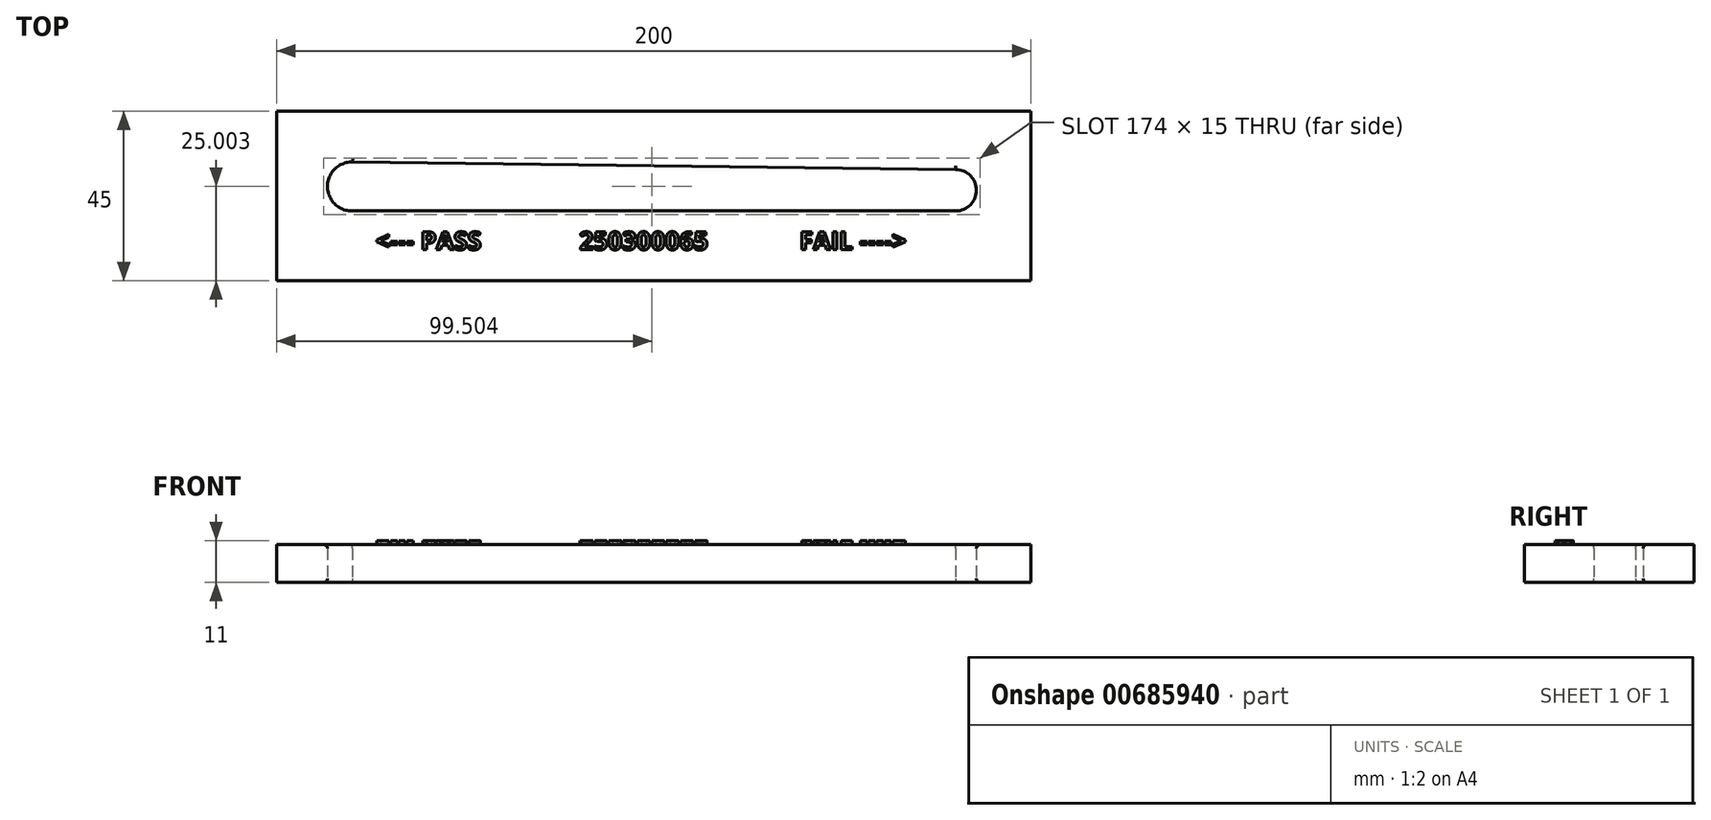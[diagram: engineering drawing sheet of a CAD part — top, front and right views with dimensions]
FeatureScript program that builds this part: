
annotation { "Feature Type Name" : "Feature", "Feature Type Description" : "" }
export const myFeature = defineFeature(function(context is Context, id is Id, definition is map)
    precondition{}
    {
        {
            var Q0;
            Q0=qCreatedBy(makeId("Top.planeOp"),FACE);
            var sketch = newSketch(context, id + "F0", { "sketchPlane" : qUnion([Q0])});
            skLineSegment(sketch, "E0", {"start": v(-35.7, 23.28) * mm, "end": v(124.3, 21.28) * mm});
            skLineSegment(sketch, "E1", {"start": v(-35.7, 10.28) * mm, "end": v(124.3, 10.28) * mm});
            skArc(sketch, "E2", {"start": v(-35.54, 23.28) * mm, "mid": v(-42.2, 16.87) * mm, "end": v(-35.7, 10.28) * mm});
            skArc(sketch, "E3", {"start": v(124.3, 10.28) * mm, "mid": v(129.8, 15.78) * mm, "end": v(124.3, 21.28) * mm});
            skLineSegment(sketch, "E4.bottom", {"start": v(-55.7, 36.78) * mm, "end": v(144.3, 36.78) * mm});
            skLineSegment(sketch, "E4.top", {"start": v(-55.7, -8.22) * mm, "end": v(144.3, -8.22) * mm});
            skLineSegment(sketch, "E4.left", {"start": v(-55.7, 36.78) * mm, "end": v(-55.7, -8.22) * mm});
            skLineSegment(sketch, "E4.right", {"start": v(144.3, 36.78) * mm, "end": v(144.3, -8.22) * mm});
            skSolve(sketch);
        }
        {
            var Q0;
            Q0 = qSketchRegion(id + "F0", true);
            extrude(context, id + "F1", {"entities" : qUnion([Q0]), "depth" : 10 * mm, "offsetDistance" : 25 * mm});
        }
        {
            var Q0;
            Q0=makeQuery(id+"F1.opExtrude","CAP_EDGE",EDGE,{"disambiguationData":[OSD([sQuery(id+"F0.wireOp",EDGE,"E0")])],"isStart":false});
            var Q1;
            Q1=makeQuery(id+"F1.opExtrude","CAP_EDGE",EDGE,{"disambiguationData":[OSD([sQuery(id+"F0.wireOp",EDGE,"E2")])],"isStart":false});
            var Q2;
            Q2=makeQuery(id+"F1.opExtrude","CAP_EDGE",EDGE,{"disambiguationData":[OSD([sQuery(id+"F0.wireOp",EDGE,"E1")])],"isStart":false});
            var Q3;
            Q3=makeQuery(id+"F1.opExtrude","CAP_EDGE",EDGE,{"disambiguationData":[OSD([sQuery(id+"F0.wireOp",EDGE,"E3")])],"isStart":false});
            fillet(context, id + "F2", {"entities" : qUnion([Q0, Q1, Q2, Q3]), "radius" : 1 * mm, "tangentPropagation" : true, "allowEdgeOverflow" : false});
        }
        {
            var Q0;
            Q0=makeQuery(id+"F1.opExtrude","CAP_EDGE",EDGE,{"disambiguationData":[OSD([sQuery(id+"F0.wireOp",EDGE,"E0")])],"isStart":true});
            var Q1;
            Q1=makeQuery(id+"F1.opExtrude","CAP_EDGE",EDGE,{"disambiguationData":[OSD([sQuery(id+"F0.wireOp",EDGE,"E3")])],"isStart":true});
            var Q2;
            Q2=makeQuery(id+"F1.opExtrude","CAP_EDGE",EDGE,{"disambiguationData":[OSD([sQuery(id+"F0.wireOp",EDGE,"E1")])],"isStart":true});
            fillet(context, id + "F3", {"entities" : qUnion([Q0, Q1, Q2]), "radius" : 1 * mm, "tangentPropagation" : true, "allowEdgeOverflow" : false});
        }
        {
            var Q0;
            Q0=makeQuery(id+"F1.opExtrude","CAP_FACE",FACE,{"disambiguationData":[OSD([sQuery(id+"F0.wireOp",EDGE,"E0"),sQuery(id+"F0.wireOp",EDGE,"E1"),sQuery(id+"F0.wireOp",EDGE,"E2"),sQuery(id+"F0.wireOp",EDGE,"E3"),sQuery(id+"F0.wireOp",EDGE,"E4.bottom"),sQuery(id+"F0.wireOp",EDGE,"E4.top"),sQuery(id+"F0.wireOp",EDGE,"E4.left"),sQuery(id+"F0.wireOp",EDGE,"E4.right")])],"isStart":false});
            var sketch = newSketch(context, id + "F4", { "sketchPlane" : qUnion([Q0])});
            skText(sketch, "E5", { "text": "<--- PASS               250300065              FAIL ---->", "fontName": "OpenSans-Bold.ttf"});
            const initialGuessF4  = {"E5": [-0.02945, 0, 1, 0, 0.00479]};
            skSetInitialGuess(sketch, initialGuessF4);
            skSolve(sketch);
        }
        {
            var Q0;
            Q0 = qSketchRegion(id + "F4", true);
            extrude(context, id + "F5", {"entities" : qUnion([Q0]), "operationType" : NewBodyOperationType.ADD, "depth" : 1 * mm, "offsetDistance" : 25 * mm});
        }
    });
